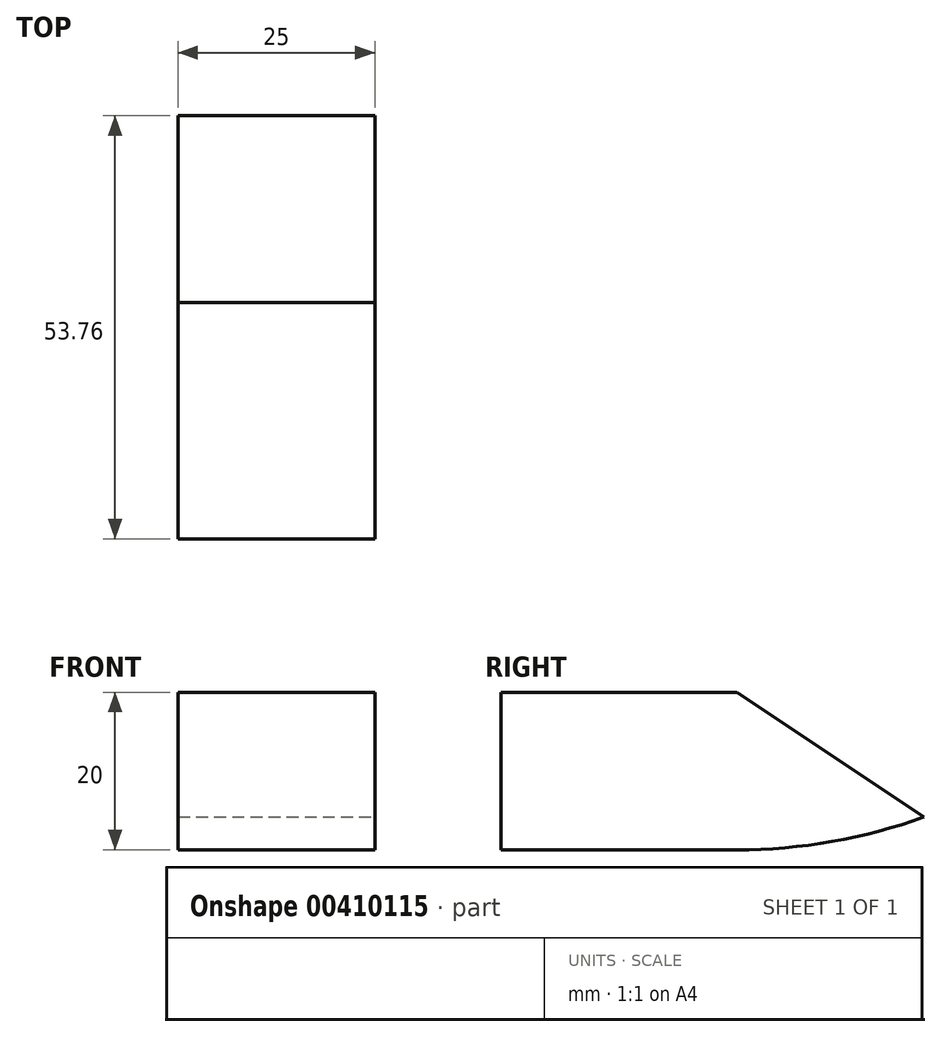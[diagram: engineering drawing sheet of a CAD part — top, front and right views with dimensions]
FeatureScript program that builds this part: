
annotation { "Feature Type Name" : "Feature", "Feature Type Description" : "" }
export const myFeature = defineFeature(function(context is Context, id is Id, definition is map)
    precondition{}
    {
        {
            var Q0;
            Q0=qCreatedBy(makeId("Right.planeOp"),FACE);
            var sketch = newSketch(context, id + "F0", { "sketchPlane" : qUnion([Q0])});
            skLineSegment(sketch, "E0.bottom", {"start": v(0, 0) * mm, "end": v(30, 0) * mm});
            skLineSegment(sketch, "E0.top", {"start": v(0, -20) * mm, "end": v(60, -20) * mm});
            skLineSegment(sketch, "E0.left", {"start": v(0, 0) * mm, "end": v(0, -20) * mm});
            skLineSegment(sketch, "E1", {"start": v(60, -20) * mm, "end": v(30, 0) * mm});
            skPoint(sketch, "E2.orphan", {"position": v(60, 0) * mm});
            skSolve(sketch);
        }
        {
            var Q0;
            Q0 = qSketchRegion(id + "F0", true);
            extrude(context, id + "F1", {"entities" : qUnion([Q0]), "depth" : 25 * mm});
        }
        {
            var Q0;
            Q0=makeQuery(id+"F1.opExtrude","CAP_FACE",FACE,{"disambiguationData":[OSD([sQuery(id+"F0.wireOp",EDGE,"E0.bottom"),sQuery(id+"F0.wireOp",EDGE,"E0.top"),sQuery(id+"F0.wireOp",EDGE,"E0.left"),sQuery(id+"F0.wireOp",EDGE,"E1")])],"isStart":false});
            var sketch = newSketch(context, id + "F2", { "sketchPlane" : qUnion([Q0])});
            skLineSegment(sketch, "E3", {"start": v(0, -20) * mm, "end": v(30, -20) * mm});
            skArc(sketch, "E4", {"start": v(30, -20) * mm, "mid": v(42.06, -18.95) * mm, "end": v(53.76, -15.84) * mm});
            skLineSegment(sketch, "E5", {"start": v(0, -20) * mm, "end": v(0, -28) * mm});
            skLineSegment(sketch, "E6", {"start": v(0, -28) * mm, "end": v(72, -28) * mm});
            skLineSegment(sketch, "E7", {"start": v(53.76, -15.84) * mm, "end": v(72, -28) * mm});
            skSolve(sketch);
        }
        {
            var Q0;
            Q0 = qSketchRegion(id + "F2", true);
            extrude(context, id + "F3", {"entities" : qUnion([Q0]), "operationType" : NewBodyOperationType.REMOVE, "oppositeDirection" : true, "depth" : 25 * mm});
        }
    });
